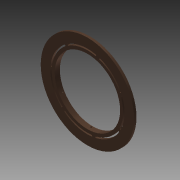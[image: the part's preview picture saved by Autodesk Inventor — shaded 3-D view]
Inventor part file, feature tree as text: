
AUTODESK INVENTOR PART (.ipt)
format: ipt  version: 2015 (Build 190159000, 159)  size: 249,856 bytes
history: native  units: in
note: dims shown in document units (in); Inventor stores cm internally (conversion verified against a paired STEP export)
features: sketch x6, extrude x5, plane x2, pattern_circular x1, reference x1, projected_geometry x1
ambient origin geometry x8: Origin, YZ Plane, XZ Plane, XY Plane, X Axis, Y Axis, Z Axis, Center Point
bodies: Solid1 (feature_tree)
feature tree (16):
  plane  "Work Plane1"
  extrude  "Extrusion1"  Depth=0.4331in TaperAngle=0.0deg
  extrude  "Extrusion2"  Depth=0.1181in
  extrude  "Extrusion3"  Depth=2.7559in TaperAngle=360.0deg
  extrude  "Extrusion4"  Depth=5.5118in
  sketch  "Sketch5"  dims[d17=5.7874in d18=8.2677in]
  plane  "Work Plane2"
  extrude  "Extrusion5"  Depth=8.2677in
  pattern_circular  "Circular Pattern1"  Count=20  [1 undecoded]
  sketch  "Sketch1"  dims[d0=0.1575in d2=0.4331in d3=0.0in]
  sketch  "Sketch2"  dims[d4=0.1969in d5=0.0in d7=0.1181in]
  reference  "Reference2"
  sketch  "Sketch3"  dims[d8=45.0deg d10=2.7559in d12=360.0deg]
  sketch  "Sketch4"  dims[d14=0.4331in d15=0.0in d16=5.5118in]
  sketch  "Sketch6"  dims[d19=0.2362in d20=0.0in d21=7.874in d22=3.0709in d23=0.315in d24=0.1181in d25=0.2362in d26=0.0in d27=0.1181in d28=0.0in d29=2.3622in d30=360.0deg]
  projected_geometry  "Projected Loop1"
note: 1 required parameter value undecoded (feature->parameter linkage not recoverable at this tier; creation-order binding heuristic only, values carry confidence <= 0.55)
